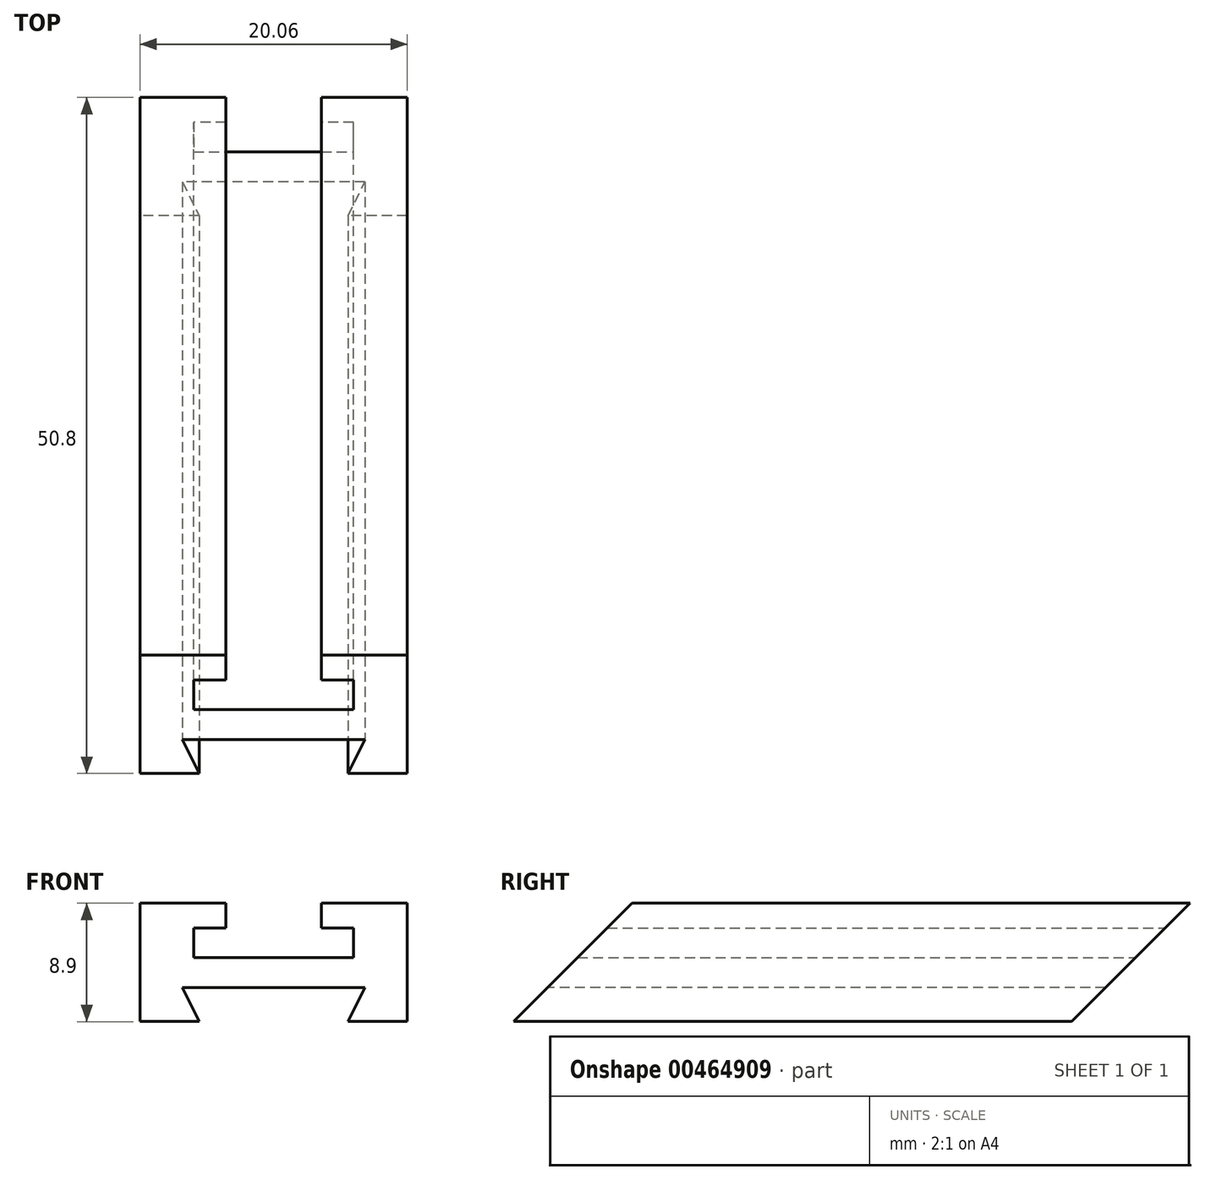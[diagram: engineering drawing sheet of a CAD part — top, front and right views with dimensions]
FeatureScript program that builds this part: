
annotation { "Feature Type Name" : "Feature", "Feature Type Description" : "" }
export const myFeature = defineFeature(function(context is Context, id is Id, definition is map)
    precondition{}
    {
        {
            var Q0;
            Q0=qCreatedBy(makeId("Right.planeOp"),FACE);
            var sketch = newSketch(context, id + "F0", { "sketchPlane" : qUnion([Q0])});
            skLineSegment(sketch, "E0.bottom", {"start": v(25.4, 4.45) * mm, "end": v(-16.51, 4.44) * mm});
            skLineSegment(sketch, "E0.top", {"start": v(16.51, -4.44) * mm, "end": v(-25.4, -4.45) * mm});
            skPoint(sketch, "E0.middle", {"position": v(0, 0) * mm});
            skLineSegment(sketch, "E1", {"start": v(-25.4, -4.45) * mm, "end": v(-16.51, 4.44) * mm});
            skLineSegment(sketch, "E2", {"start": v(25.4, 4.45) * mm, "end": v(16.51, -4.44) * mm});
            skSolve(sketch);
        }
        {
            var Q0;
            Q0 = qSketchRegion(id + "F0", true);
            extrude(context, id + "F1", {"entities" : qUnion([Q0]), "endBound" : BoundingType.SYMMETRIC, "depth" : 20.07 * mm});
        }
        {
            var Q0;
            Q0=qCreatedBy(makeId("Front.planeOp"),FACE);
            var sketch = newSketch(context, id + "F2", { "sketchPlane" : qUnion([Q0])});
            skLineSegment(sketch, "E3", {"start": v(-3.6, 7.68) * mm, "end": v(-3.6, 2.6) * mm});
            skLineSegment(sketch, "E4", {"start": v(-3.6, 2.6) * mm, "end": v(-6, 2.6) * mm});
            skLineSegment(sketch, "E5", {"start": v(-6, 2.6) * mm, "end": v(-6, 0.37) * mm});
            skLineSegment(sketch, "E6", {"start": v(-6, 0.37) * mm, "end": v(6, 0.37) * mm});
            skLineSegment(sketch, "E7", {"start": v(6, 0.37) * mm, "end": v(6, 2.6) * mm});
            skLineSegment(sketch, "E8", {"start": v(6, 2.6) * mm, "end": v(3.6, 2.6) * mm});
            skLineSegment(sketch, "E9", {"start": v(3.6, 2.6) * mm, "end": v(3.6, 7.68) * mm});
            skLineSegment(sketch, "E10", {"start": v(3.6, 7.68) * mm, "end": v(-3.6, 7.68) * mm});
            skLineSegment(sketch, "E11", {"start": v(0, -9.28) * mm, "end": v(0, 7.33) * mm, "construction": true});
            skSolve(sketch);
        }
        {
            var Q0;
            Q0 = qSketchRegion(id + "F2", true);
            extrude(context, id + "F3", {"entities" : qUnion([Q0]), "operationType" : NewBodyOperationType.REMOVE, "endBound" : BoundingType.SYMMETRIC, "depth" : 152.4 * mm});
        }
        {
            var Q0;
            Q0=qCreatedBy(makeId("Front.planeOp"),FACE);
            var sketch = newSketch(context, id + "F4", { "sketchPlane" : qUnion([Q0])});
            skLineSegment(sketch, "E12", {"start": v(0, 1.15) * mm, "end": v(0, -10.33) * mm, "construction": true});
            skLineSegment(sketch, "E13", {"start": v(-5.59, -4.45) * mm, "end": v(-6.86, -1.9) * mm});
            skLineSegment(sketch, "E14", {"start": v(-6.86, -1.9) * mm, "end": v(6.86, -1.9) * mm});
            skLineSegment(sketch, "E15", {"start": v(6.86, -1.9) * mm, "end": v(5.59, -4.45) * mm});
            skLineSegment(sketch, "E16", {"start": v(5.59, -4.45) * mm, "end": v(-5.59, -4.45) * mm});
            skSolve(sketch);
        }
        {
            var Q0;
            Q0 = qSketchRegion(id + "F4", true);
            extrude(context, id + "F5", {"entities" : qUnion([Q0]), "operationType" : NewBodyOperationType.REMOVE, "endBound" : BoundingType.SYMMETRIC, "oppositeDirection" : true, "depth" : 152.4 * mm});
        }
    });
